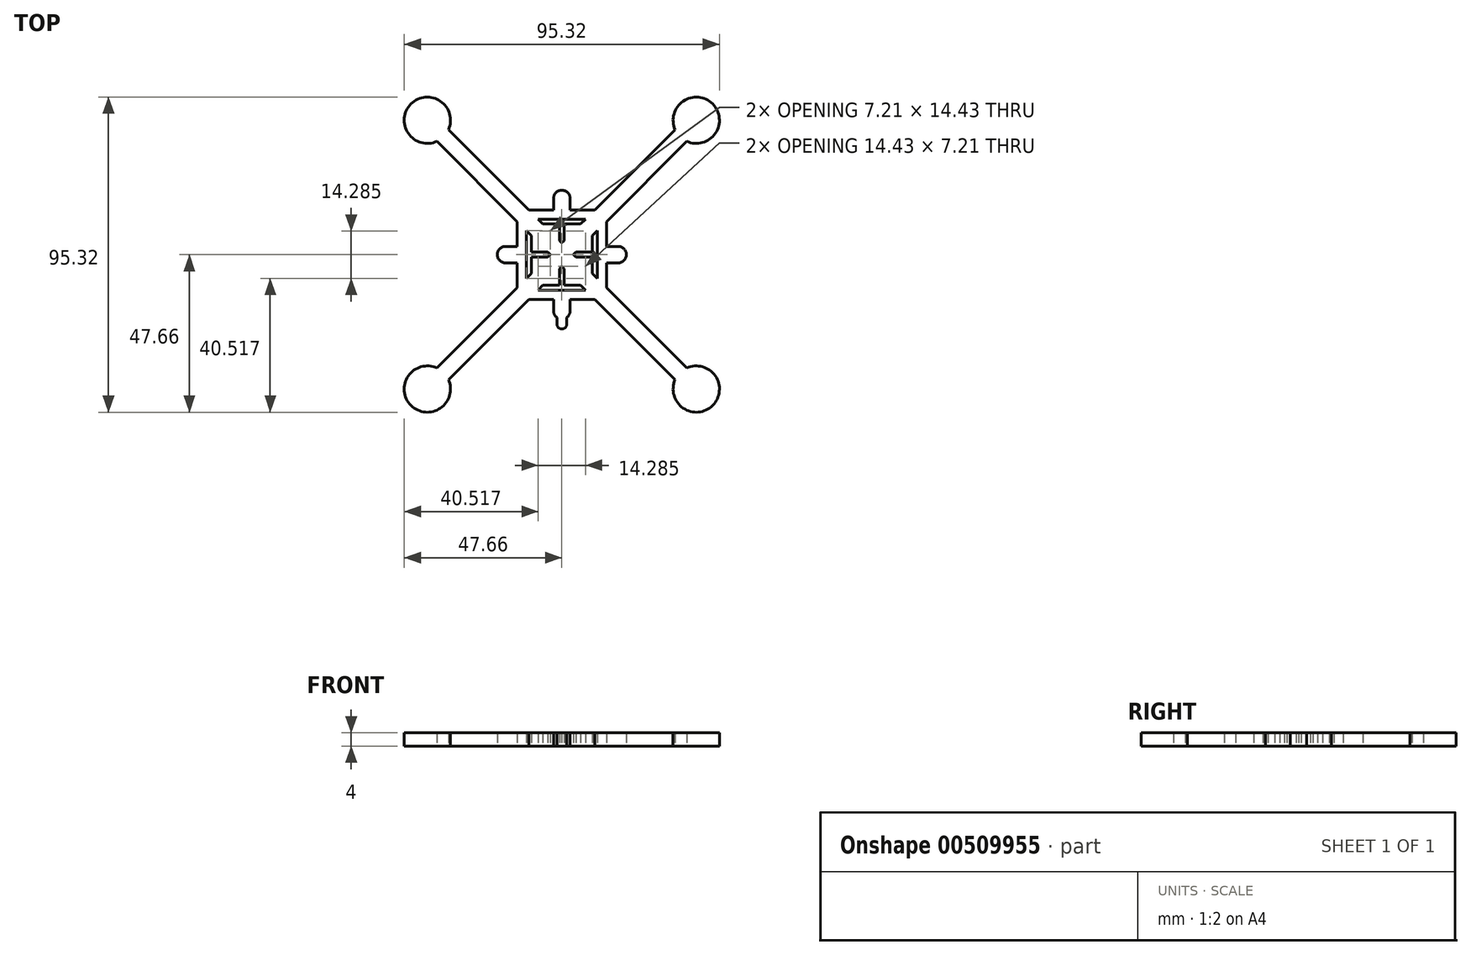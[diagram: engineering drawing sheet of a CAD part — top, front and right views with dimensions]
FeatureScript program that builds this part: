
annotation { "Feature Type Name" : "Feature", "Feature Type Description" : "" }
export const myFeature = defineFeature(function(context is Context, id is Id, definition is map)
    precondition{}
    {
        {
            var Q0;
            Q0=qCreatedBy(makeId("Top.planeOp"),FACE);
            var sketch = newSketch(context, id + "F0", { "sketchPlane" : qUnion([Q0])});
            skLineSegment(sketch, "E0", {"start": v(-40.66, 40.66) * mm, "end": v(40.66, -40.66) * mm});
            skLineSegment(sketch, "E1", {"start": v(40.66, 40.66) * mm, "end": v(-40.66, -40.66) * mm});
            skLineSegment(sketch, "E2.bottom", {"start": v(-13.5, 13.5) * mm, "end": v(13.5, 13.5) * mm});
            skLineSegment(sketch, "E2.top", {"start": v(-13.5, -13.5) * mm, "end": v(13.5, -13.5) * mm});
            skLineSegment(sketch, "E2.left", {"start": v(-13.5, 13.5) * mm, "end": v(-13.5, -13.5) * mm});
            skLineSegment(sketch, "E2.right", {"start": v(13.5, 13.5) * mm, "end": v(13.5, -13.5) * mm});
            skPoint(sketch, "E2.middle", {"position": v(0, 0) * mm});
            skCircle(sketch, "E3", {"center": v(-40.66, 40.66) * mm, "radius": 7 * mm});
            skCircle(sketch, "E4", {"center": v(-40.66, -40.66) * mm, "radius": 7 * mm});
            skCircle(sketch, "E5", {"center": v(40.66, -40.66) * mm, "radius": 7 * mm});
            skCircle(sketch, "E6", {"center": v(40.66, 40.66) * mm, "radius": 7 * mm});
            skPoint(sketch, "E7", {"position": v(-10, 10) * mm});
            skPoint(sketch, "E8", {"position": v(10, 10) * mm});
            skPoint(sketch, "E9", {"position": v(10, -10) * mm});
            skPoint(sketch, "E10", {"position": v(-10, -10) * mm});
            skCircle(sketch, "E11", {"center": v(0, 17) * mm, "radius": 1.5 * mm});
            skCircle(sketch, "E12", {"center": v(-17, 0) * mm, "radius": 1.5 * mm});
            skCircle(sketch, "E13", {"center": v(0, -17) * mm, "radius": 1.5 * mm});
            skCircle(sketch, "E14", {"center": v(0, -21) * mm, "radius": 1 * mm});
            skCircle(sketch, "E15", {"center": v(17, 0) * mm, "radius": 1.5 * mm});
            skCircle(sketch, "E16", {"center": v(0, 17) * mm, "radius": 2.5 * mm});
            skCircle(sketch, "E17", {"center": v(-17, 0) * mm, "radius": 2.5 * mm});
            skCircle(sketch, "E18", {"center": v(0, -17) * mm, "radius": 2.5 * mm});
            skCircle(sketch, "E19", {"center": v(17, 0) * mm, "radius": 2.5 * mm});
            skLineSegment(sketch, "E20", {"start": v(-2.5, 17) * mm, "end": v(-2.5, 13.5) * mm});
            skLineSegment(sketch, "E21", {"start": v(2.5, 17) * mm, "end": v(2.5, 13.5) * mm});
            skLineSegment(sketch, "E22", {"start": v(17, 2.5) * mm, "end": v(13.5, 2.5) * mm});
            skLineSegment(sketch, "E23", {"start": v(17, -2.5) * mm, "end": v(13.5, -2.5) * mm});
            skLineSegment(sketch, "E24", {"start": v(2.5, -17) * mm, "end": v(2.5, -13.5) * mm});
            skLineSegment(sketch, "E25", {"start": v(-2.5, -17) * mm, "end": v(-2.5, -13.5) * mm});
            skLineSegment(sketch, "E26", {"start": v(-17, -2.5) * mm, "end": v(-13.5, -2.5) * mm});
            skLineSegment(sketch, "E27", {"start": v(-17, 2.5) * mm, "end": v(-13.5, 2.5) * mm});
            skCircle(sketch, "E28", {"center": v(0, -21) * mm, "radius": 1.5 * mm});
            skLineSegment(sketch, "E29", {"start": v(-1.5, -21) * mm, "end": v(-1.5, -19) * mm});
            skLineSegment(sketch, "E30", {"start": v(1.5, -21) * mm, "end": v(1.5, -19) * mm});
            skLineSegment(sketch, "E31.0", {"start": v(38.9, 42.43) * mm, "end": v(-42.43, -38.9) * mm});
            skLineSegment(sketch, "E32.0", {"start": v(42.43, 38.9) * mm, "end": v(-38.9, -42.43) * mm});
            skLineSegment(sketch, "E33.0", {"start": v(-42.43, 38.9) * mm, "end": v(38.9, -42.43) * mm});
            skLineSegment(sketch, "E34.0", {"start": v(-38.9, 42.43) * mm, "end": v(42.43, -38.9) * mm});
            skLineSegment(sketch, "E35", {"start": v(-42.43, -38.9) * mm, "end": v(-40.66, -40.66) * mm});
            skLineSegment(sketch, "E36", {"start": v(-38.9, -42.43) * mm, "end": v(-40.66, -40.66) * mm});
            skLineSegment(sketch, "E37", {"start": v(38.9, 42.43) * mm, "end": v(40.66, 40.66) * mm});
            skLineSegment(sketch, "E38", {"start": v(40.66, 40.66) * mm, "end": v(42.43, 38.9) * mm});
            skLineSegment(sketch, "E39", {"start": v(42.43, -38.9) * mm, "end": v(40.66, -40.66) * mm});
            skLineSegment(sketch, "E40", {"start": v(40.66, -40.66) * mm, "end": v(38.9, -42.43) * mm});
            skLineSegment(sketch, "E41", {"start": v(-38.9, 42.43) * mm, "end": v(-40.66, 40.66) * mm});
            skLineSegment(sketch, "E42", {"start": v(-40.66, 40.66) * mm, "end": v(-42.43, 38.9) * mm});
            skPoint(sketch, "E43", {"position": v(-40.66, 45.16) * mm});
            skPoint(sketch, "E44.1.0", {"position": v(-45.16, 40.66) * mm});
            skPoint(sketch, "E44.2.0", {"position": v(-40.66, 36.16) * mm});
            skPoint(sketch, "E45.0.3.0", {"position": v(-36.16, 40.66) * mm});
            skPoint(sketch, "E46", {"position": v(40.66, 45.16) * mm});
            skPoint(sketch, "E47.1.0", {"position": v(36.16, 40.66) * mm});
            skPoint(sketch, "E47.2.0", {"position": v(40.66, 36.16) * mm});
            skLineSegment(sketch, "E47.anchor1", {"start": v(40.66, 40.66) * mm, "end": v(40.66, 45.16) * mm, "construction": true});
            skLineSegment(sketch, "E47.anchor2", {"start": v(40.66, 40.66) * mm, "end": v(45.16, 40.66) * mm, "construction": true});
            skPoint(sketch, "E48.0.3.0", {"position": v(45.16, 40.66) * mm});
            skPoint(sketch, "E49", {"position": v(40.66, -45.16) * mm});
            skPoint(sketch, "E50.1.0", {"position": v(36.16, -40.66) * mm});
            skPoint(sketch, "E50.2.0", {"position": v(40.66, -36.16) * mm});
            skPoint(sketch, "E50.3.0", {"position": v(45.16, -40.66) * mm});
            skLineSegment(sketch, "E50.anchor1", {"start": v(40.66, -40.66) * mm, "end": v(40.66, -45.16) * mm, "construction": true});
            skLineSegment(sketch, "E50.anchor2", {"start": v(40.66, -40.66) * mm, "end": v(45.16, -40.66) * mm, "construction": true});
            skPoint(sketch, "E51", {"position": v(-40.66, -45.16) * mm});
            skPoint(sketch, "E52.1.0", {"position": v(-45.16, -40.66) * mm});
            skPoint(sketch, "E52.2.0", {"position": v(-40.66, -36.16) * mm});
            skPoint(sketch, "E52.3.0", {"position": v(-36.16, -40.66) * mm});
            skLineSegment(sketch, "E52.anchor1", {"start": v(-40.66, -40.66) * mm, "end": v(-40.66, -45.16) * mm, "construction": true});
            skLineSegment(sketch, "E52.anchor2", {"start": v(-40.66, -40.66) * mm, "end": v(-36.16, -40.66) * mm, "construction": true});
            skLineSegment(sketch, "E53.bottom", {"start": v(10.75, -10.75) * mm, "end": v(-10.75, -10.75) * mm});
            skLineSegment(sketch, "E53.top", {"start": v(10.75, 10.75) * mm, "end": v(-10.75, 10.75) * mm});
            skLineSegment(sketch, "E53.left", {"start": v(10.75, -10.75) * mm, "end": v(10.75, 10.75) * mm});
            skLineSegment(sketch, "E53.right", {"start": v(-10.75, -10.75) * mm, "end": v(-10.75, 10.75) * mm});
            skLineSegment(sketch, "E54.bottom", {"start": v(-9.25, -9.25) * mm, "end": v(9.25, -9.25) * mm});
            skLineSegment(sketch, "E54.top", {"start": v(-9.25, 9.25) * mm, "end": v(9.25, 9.25) * mm});
            skLineSegment(sketch, "E54.left", {"start": v(-9.25, -9.25) * mm, "end": v(-9.25, 9.25) * mm});
            skLineSegment(sketch, "E54.right", {"start": v(9.25, -9.25) * mm, "end": v(9.25, 9.25) * mm});
            skLineSegment(sketch, "E55.bottom", {"start": v(-0.75, 9.25) * mm, "end": v(0.75, 9.25) * mm});
            skLineSegment(sketch, "E55.top", {"start": v(-0.75, -9.25) * mm, "end": v(0.75, -9.25) * mm});
            skLineSegment(sketch, "E55.left", {"start": v(-0.75, 9.25) * mm, "end": v(-0.75, -9.25) * mm});
            skLineSegment(sketch, "E55.right", {"start": v(0.75, 9.25) * mm, "end": v(0.75, -9.25) * mm});
            skLineSegment(sketch, "E56.bottom", {"start": v(-9.25, -0.75) * mm, "end": v(9.25, -0.75) * mm});
            skLineSegment(sketch, "E56.top", {"start": v(-9.25, 0.75) * mm, "end": v(9.25, 0.75) * mm});
            skLineSegment(sketch, "E56.left", {"start": v(-9.25, -0.75) * mm, "end": v(-9.25, 0.75) * mm});
            skLineSegment(sketch, "E56.right", {"start": v(9.25, -0.75) * mm, "end": v(9.25, 0.75) * mm});
            skPoint(sketch, "E56.cornerSnap0", {"position": v(-1.77, -0.75) * mm});
            skSolve(sketch);
        }
        {
            var Q0;
            {var subQ0=sQuery(id+"F0.wireOp",EDGE,"E39");Q0=makeQuery(id+"F0.imprint","IMPRINT",FACE,{"disambiguationData":[TD([[makeQuery(id+"F0.imprint","IMPRINT",EDGE,{"derivedFrom":subQ0}),1.0]])]});}
            var Q1;
            {var subQ3=sQuery(id+"F0.wireOp",EDGE,"E5");var subQ5=sQuery(id+"F0.wireOp",EDGE,"E33.0");var subQ7=makeQuery(id+"F0.imprint","INTERSECT",VERTEX,{"derivedFrom":[subQ3,subQ5]});Q1=makeQuery(id+"F0.imprint","IMPRINT",FACE,{"disambiguationData":[TD([[makeQuery(id+"F0.imprint","IMPRINT",EDGE,{"disambiguationData":[TD([[subQ7,1.0]])],"derivedFrom":subQ3}),-1.0]])]});}
            var Q2;
            {var subQ0=sQuery(id+"F0.wireOp",EDGE,"E56.bottom");var subQ1=sQuery(id+"F0.wireOp",EDGE,"E34.0");var subQ2=makeQuery(id+"F0.imprint","INTERSECT",VERTEX,{"derivedFrom":[subQ1,subQ0]});Q2=makeQuery(id+"F0.imprint","IMPRINT",FACE,{"disambiguationData":[TD([[makeQuery(id+"F0.imprint","IMPRINT",EDGE,{"disambiguationData":[TD([[subQ2,-1.0]])],"derivedFrom":subQ1}),1.0]])]});}
            var Q3;
            {var subQ3=sQuery(id+"F0.wireOp",EDGE,"E4");var subQ5=sQuery(id+"F0.wireOp",EDGE,"E32.0");var subQ6=makeQuery(id+"F0.imprint","INTERSECT",VERTEX,{"derivedFrom":[subQ3,subQ5]});Q3=makeQuery(id+"F0.imprint","IMPRINT",FACE,{"disambiguationData":[TD([[makeQuery(id+"F0.imprint","IMPRINT",EDGE,{"disambiguationData":[TD([[subQ6,-1.0]])],"derivedFrom":subQ3}),-1.0]])]});}
            var Q4;
            {var subQ0=sQuery(id+"F0.wireOp",EDGE,"E41");Q4=makeQuery(id+"F0.imprint","IMPRINT",FACE,{"disambiguationData":[TD([[makeQuery(id+"F0.imprint","IMPRINT",EDGE,{"derivedFrom":subQ0}),-1.0]])]});}
            var Q5;
            {var subQ3=sQuery(id+"F0.wireOp",EDGE,"E5");var subQ5=sQuery(id+"F0.wireOp",EDGE,"E34.0");var subQ7=makeQuery(id+"F0.imprint","INTERSECT",VERTEX,{"derivedFrom":[subQ3,subQ5]});Q5=makeQuery(id+"F0.imprint","IMPRINT",FACE,{"disambiguationData":[TD([[makeQuery(id+"F0.imprint","IMPRINT",EDGE,{"disambiguationData":[TD([[subQ7,-1.0]])],"derivedFrom":subQ3}),-1.0]])]});}
            var Q6;
            {var subQ3=sQuery(id+"F0.wireOp",EDGE,"E4");var subQ5=sQuery(id+"F0.wireOp",EDGE,"E31.0");var subQ7=makeQuery(id+"F0.imprint","INTERSECT",VERTEX,{"derivedFrom":[subQ3,subQ5]});Q6=makeQuery(id+"F0.imprint","IMPRINT",FACE,{"disambiguationData":[TD([[makeQuery(id+"F0.imprint","IMPRINT",EDGE,{"disambiguationData":[TD([[subQ7,1.0]])],"derivedFrom":subQ3}),-1.0]])]});}
            var Q7;
            {var subQ3=sQuery(id+"F0.wireOp",EDGE,"E31.0");var subQ5=sQuery(id+"F0.wireOp",EDGE,"E56.bottom");var subQ6=makeQuery(id+"F0.imprint","INTERSECT",VERTEX,{"derivedFrom":[subQ3,subQ5]});Q7=makeQuery(id+"F0.imprint","IMPRINT",FACE,{"disambiguationData":[TD([[makeQuery(id+"F0.imprint","IMPRINT",EDGE,{"disambiguationData":[TD([[subQ6,-1.0]])],"derivedFrom":subQ3}),1.0]])]});}
            var Q8;
            {var subQ1=sQuery(id+"F0.wireOp",EDGE,"E2.bottom");var subQ6=makeQuery(id+"F0.imprint","INTERSECT",VERTEX,{"derivedFrom":[subQ1,sQuery(id+"F0.wireOp",EDGE,"E20")]});Q8=makeQuery(id+"F0.imprint","IMPRINT",FACE,{"disambiguationData":[TD([[makeQuery(id+"F0.imprint","IMPRINT",EDGE,{"disambiguationData":[TD([[subQ6,1.0]])],"derivedFrom":subQ1}),-1.0]])]});}
            var Q9;
            {var subQ4=sQuery(id+"F0.wireOp",EDGE,"E35");Q9=makeQuery(id+"F0.imprint","IMPRINT",FACE,{"disambiguationData":[TD([[makeQuery(id+"F0.imprint","IMPRINT",EDGE,{"derivedFrom":subQ4}),-1.0]])]});}
            var Q10;
            {var subQ0=sQuery(id+"F0.wireOp",EDGE,"E56.right");Q10=makeQuery(id+"F0.imprint","IMPRINT",FACE,{"disambiguationData":[TD([[makeQuery(id+"F0.imprint","IMPRINT",EDGE,{"derivedFrom":subQ0}),-1.0]])]});}
            var Q11;
            {var subQ1=sQuery(id+"F0.wireOp",EDGE,"E2.right");var subQ8=makeQuery(id+"F0.imprint","INTERSECT",VERTEX,{"derivedFrom":[subQ1,sQuery(id+"F0.wireOp",EDGE,"E22")]});Q11=makeQuery(id+"F0.imprint","IMPRINT",FACE,{"disambiguationData":[TD([[makeQuery(id+"F0.imprint","IMPRINT",EDGE,{"disambiguationData":[TD([[subQ8,1.0]])],"derivedFrom":subQ1}),-1.0]])]});}
            var Q12;
            {var subQ0=sQuery(id+"F0.wireOp",EDGE,"E37");Q12=makeQuery(id+"F0.imprint","IMPRINT",FACE,{"disambiguationData":[TD([[makeQuery(id+"F0.imprint","IMPRINT",EDGE,{"derivedFrom":subQ0}),1.0]])]});}
            var Q13;
            {var subQ3=sQuery(id+"F0.wireOp",EDGE,"E6");var subQ5=sQuery(id+"F0.wireOp",EDGE,"E31.0");var subQ7=makeQuery(id+"F0.imprint","INTERSECT",VERTEX,{"derivedFrom":[subQ3,subQ5]});Q13=makeQuery(id+"F0.imprint","IMPRINT",FACE,{"disambiguationData":[TD([[makeQuery(id+"F0.imprint","IMPRINT",EDGE,{"disambiguationData":[TD([[subQ7,-1.0]])],"derivedFrom":subQ3}),-1.0]])]});}
            var Q14;
            {var subQ3=sQuery(id+"F0.wireOp",EDGE,"E3");var subQ5=sQuery(id+"F0.wireOp",EDGE,"E34.0");var subQ7=makeQuery(id+"F0.imprint","INTERSECT",VERTEX,{"derivedFrom":[subQ3,subQ5]});Q14=makeQuery(id+"F0.imprint","IMPRINT",FACE,{"disambiguationData":[TD([[makeQuery(id+"F0.imprint","IMPRINT",EDGE,{"disambiguationData":[TD([[subQ7,1.0]])],"derivedFrom":subQ3}),-1.0]])]});}
            var Q15;
            {var subQ3=sQuery(id+"F0.wireOp",EDGE,"E6");var subQ5=sQuery(id+"F0.wireOp",EDGE,"E32.0");var subQ7=makeQuery(id+"F0.imprint","INTERSECT",VERTEX,{"derivedFrom":[subQ3,subQ5]});Q15=makeQuery(id+"F0.imprint","IMPRINT",FACE,{"disambiguationData":[TD([[makeQuery(id+"F0.imprint","IMPRINT",EDGE,{"disambiguationData":[TD([[subQ7,1.0]])],"derivedFrom":subQ3}),-1.0]])]});}
            var Q16;
            {var subQ1=sQuery(id+"F0.wireOp",EDGE,"E0");var subQ7=sQuery(id+"F0.wireOp",EDGE,"E31.0");var subQ8=makeQuery(id+"F0.imprint","INTERSECT",VERTEX,{"derivedFrom":[subQ1,subQ7]});Q16=makeQuery(id+"F0.imprint","IMPRINT",FACE,{"disambiguationData":[TD([[makeQuery(id+"F0.imprint","IMPRINT",EDGE,{"disambiguationData":[TD([[subQ8,1.0]])],"derivedFrom":subQ7}),-1.0]])]});}
            var Q17;
            {var subQ1=sQuery(id+"F0.wireOp",EDGE,"E2.left");var subQ6=makeQuery(id+"F0.imprint","INTERSECT",VERTEX,{"derivedFrom":[subQ1,sQuery(id+"F0.wireOp",EDGE,"E27")]});Q17=makeQuery(id+"F0.imprint","IMPRINT",FACE,{"disambiguationData":[TD([[makeQuery(id+"F0.imprint","IMPRINT",EDGE,{"disambiguationData":[TD([[subQ6,1.0]])],"derivedFrom":subQ1}),1.0]])]});}
            var Q18;
            {var subQ3=sQuery(id+"F0.wireOp",EDGE,"E3");var subQ5=sQuery(id+"F0.wireOp",EDGE,"E33.0");var subQ7=makeQuery(id+"F0.imprint","INTERSECT",VERTEX,{"derivedFrom":[subQ3,subQ5]});Q18=makeQuery(id+"F0.imprint","IMPRINT",FACE,{"disambiguationData":[TD([[makeQuery(id+"F0.imprint","IMPRINT",EDGE,{"disambiguationData":[TD([[subQ7,-1.0]])],"derivedFrom":subQ3}),-1.0]])]});}
            var Q19;
            {var subQ1=sQuery(id+"F0.wireOp",EDGE,"E0");var subQ5=sQuery(id+"F0.wireOp",EDGE,"E32.0");var subQ6=makeQuery(id+"F0.imprint","INTERSECT",VERTEX,{"derivedFrom":[subQ1,subQ5]});Q19=makeQuery(id+"F0.imprint","IMPRINT",FACE,{"disambiguationData":[TD([[makeQuery(id+"F0.imprint","IMPRINT",EDGE,{"disambiguationData":[TD([[subQ6,1.0]])],"derivedFrom":subQ5}),1.0]])]});}
            var Q20;
            {var subQ1=sQuery(id+"F0.wireOp",EDGE,"E0");var subQ7=sQuery(id+"F0.wireOp",EDGE,"E32.0");var subQ8=makeQuery(id+"F0.imprint","INTERSECT",VERTEX,{"derivedFrom":[subQ1,subQ7]});Q20=makeQuery(id+"F0.imprint","IMPRINT",FACE,{"disambiguationData":[TD([[makeQuery(id+"F0.imprint","IMPRINT",EDGE,{"disambiguationData":[TD([[subQ8,-1.0]])],"derivedFrom":subQ7}),1.0]])]});}
            var Q21;
            {var subQ0=sQuery(id+"F0.wireOp",EDGE,"E55.right");var subQ1=sQuery(id+"F0.wireOp",EDGE,"E33.0");var subQ2=makeQuery(id+"F0.imprint","INTERSECT",VERTEX,{"derivedFrom":[subQ1,subQ0]});Q21=makeQuery(id+"F0.imprint","IMPRINT",FACE,{"disambiguationData":[TD([[makeQuery(id+"F0.imprint","IMPRINT",EDGE,{"disambiguationData":[TD([[subQ2,-1.0]])],"derivedFrom":subQ1}),-1.0]])]});}
            var Q22;
            {var subQ0=sQuery(id+"F0.wireOp",EDGE,"E55.left");var subQ1=sQuery(id+"F0.wireOp",EDGE,"E32.0");var subQ2=makeQuery(id+"F0.imprint","INTERSECT",VERTEX,{"derivedFrom":[subQ1,subQ0]});Q22=makeQuery(id+"F0.imprint","IMPRINT",FACE,{"disambiguationData":[TD([[makeQuery(id+"F0.imprint","IMPRINT",EDGE,{"disambiguationData":[TD([[subQ2,-1.0]])],"derivedFrom":subQ1}),1.0]])]});}
            var Q23;
            {var subQ3=sQuery(id+"F0.wireOp",EDGE,"E55.left");var subQ7=sQuery(id+"F0.wireOp",EDGE,"E32.0");var subQ9=makeQuery(id+"F0.imprint","INTERSECT",VERTEX,{"derivedFrom":[subQ7,subQ3]});Q23=makeQuery(id+"F0.imprint","IMPRINT",FACE,{"disambiguationData":[TD([[makeQuery(id+"F0.imprint","IMPRINT",EDGE,{"disambiguationData":[TD([[subQ9,-1.0]])],"derivedFrom":subQ7}),-1.0]])]});}
            var Q24;
            {var subQ5=sQuery(id+"F0.wireOp",EDGE,"E54.right");var subQ6=sQuery(id+"F0.wireOp",EDGE,"E32.0");var subQ7=makeQuery(id+"F0.imprint","INTERSECT",VERTEX,{"derivedFrom":[subQ6,subQ5]});Q24=makeQuery(id+"F0.imprint","IMPRINT",FACE,{"disambiguationData":[TD([[makeQuery(id+"F0.imprint","IMPRINT",EDGE,{"disambiguationData":[TD([[subQ7,-1.0]])],"derivedFrom":subQ6}),-1.0]])]});}
            var Q25;
            {var subQ0=sQuery(id+"F0.wireOp",EDGE,"E54.top");var subQ3=sQuery(id+"F0.wireOp",EDGE,"E31.0");var subQ4=makeQuery(id+"F0.imprint","INTERSECT",VERTEX,{"derivedFrom":[subQ3,subQ0]});Q25=makeQuery(id+"F0.imprint","IMPRINT",FACE,{"disambiguationData":[TD([[makeQuery(id+"F0.imprint","IMPRINT",EDGE,{"disambiguationData":[TD([[subQ4,-1.0]])],"derivedFrom":subQ3}),1.0]])]});}
            var Q26;
            {var subQ0=sQuery(id+"F0.wireOp",EDGE,"E54.top");var subQ1=sQuery(id+"F0.wireOp",EDGE,"E31.0");var subQ2=makeQuery(id+"F0.imprint","INTERSECT",VERTEX,{"derivedFrom":[subQ1,subQ0]});Q26=makeQuery(id+"F0.imprint","IMPRINT",FACE,{"disambiguationData":[TD([[makeQuery(id+"F0.imprint","IMPRINT",EDGE,{"disambiguationData":[TD([[subQ2,-1.0]])],"derivedFrom":subQ1}),-1.0]])]});}
            var Q27;
            Q27=makeQuery(id+"F0.imprint","IMPRINT",FACE,{"disambiguationData":[TD([[makeQuery(id+"F0.imprint","IMPRINT",EDGE,{"derivedFrom":sQuery(id+"F0.wireOp",EDGE,"E15")}),-1.0]])]});
            var Q28;
            {var subQ0=sQuery(id+"F0.wireOp",EDGE,"E56.right");Q28=makeQuery(id+"F0.imprint","IMPRINT",FACE,{"disambiguationData":[TD([[makeQuery(id+"F0.imprint","IMPRINT",EDGE,{"derivedFrom":subQ0}),1.0]])]});}
            var Q29;
            {var subQ0=sQuery(id+"F0.wireOp",EDGE,"E40");Q29=makeQuery(id+"F0.imprint","IMPRINT",FACE,{"disambiguationData":[TD([[makeQuery(id+"F0.imprint","IMPRINT",EDGE,{"derivedFrom":subQ0}),-1.0]])]});}
            var Q30;
            {var subQ3=sQuery(id+"F0.wireOp",EDGE,"E54.right");var subQ5=sQuery(id+"F0.wireOp",EDGE,"E34.0");var subQ6=makeQuery(id+"F0.imprint","INTERSECT",VERTEX,{"derivedFrom":[subQ5,subQ3]});Q30=makeQuery(id+"F0.imprint","IMPRINT",FACE,{"disambiguationData":[TD([[makeQuery(id+"F0.imprint","IMPRINT",EDGE,{"disambiguationData":[TD([[subQ6,-1.0]])],"derivedFrom":subQ5}),-1.0]])]});}
            var Q31;
            {var subQ0=sQuery(id+"F0.wireOp",EDGE,"E36");Q31=makeQuery(id+"F0.imprint","IMPRINT",FACE,{"disambiguationData":[TD([[makeQuery(id+"F0.imprint","IMPRINT",EDGE,{"derivedFrom":subQ0}),-1.0]])]});}
            var Q32;
            {var subQ0=sQuery(id+"F0.wireOp",EDGE,"E35");Q32=makeQuery(id+"F0.imprint","IMPRINT",FACE,{"disambiguationData":[TD([[makeQuery(id+"F0.imprint","IMPRINT",EDGE,{"derivedFrom":subQ0}),1.0]])]});}
            var Q33;
            {var subQ0=sQuery(id+"F0.wireOp",EDGE,"E24");Q33=makeQuery(id+"F0.imprint","IMPRINT",FACE,{"disambiguationData":[TD([[makeQuery(id+"F0.imprint","IMPRINT",EDGE,{"derivedFrom":subQ0}),1.0]])]});}
            var Q34;
            {var subQ0=sQuery(id+"F0.wireOp",EDGE,"E55.top");Q34=makeQuery(id+"F0.imprint","IMPRINT",FACE,{"disambiguationData":[TD([[makeQuery(id+"F0.imprint","IMPRINT",EDGE,{"derivedFrom":subQ0}),-1.0]])]});}
            var Q35;
            Q35=makeQuery(id+"F0.imprint","IMPRINT",FACE,{"disambiguationData":[TD([[makeQuery(id+"F0.imprint","IMPRINT",EDGE,{"derivedFrom":sQuery(id+"F0.wireOp",EDGE,"E11")}),-1.0]])]});
            var Q36;
            {var subQ0=sQuery(id+"F0.wireOp",EDGE,"E56.left");Q36=makeQuery(id+"F0.imprint","IMPRINT",FACE,{"disambiguationData":[TD([[makeQuery(id+"F0.imprint","IMPRINT",EDGE,{"derivedFrom":subQ0}),-1.0]])]});}
            var Q37;
            {var subQ0=sQuery(id+"F0.wireOp",EDGE,"E55.right");var subQ1=sQuery(id+"F0.wireOp",EDGE,"E31.0");var subQ2=makeQuery(id+"F0.imprint","INTERSECT",VERTEX,{"derivedFrom":[subQ1,subQ0]});Q37=makeQuery(id+"F0.imprint","IMPRINT",FACE,{"disambiguationData":[TD([[makeQuery(id+"F0.imprint","IMPRINT",EDGE,{"disambiguationData":[TD([[subQ2,-1.0]])],"derivedFrom":subQ1}),1.0]])]});}
            var Q38;
            {var subQ0=sQuery(id+"F0.wireOp",EDGE,"E54.top");var subQ1=sQuery(id+"F0.wireOp",EDGE,"E34.0");var subQ2=makeQuery(id+"F0.imprint","INTERSECT",VERTEX,{"derivedFrom":[subQ1,subQ0]});Q38=makeQuery(id+"F0.imprint","IMPRINT",FACE,{"disambiguationData":[TD([[makeQuery(id+"F0.imprint","IMPRINT",EDGE,{"disambiguationData":[TD([[subQ2,-1.0]])],"derivedFrom":subQ1}),1.0]])]});}
            var Q39;
            {var subQ0=sQuery(id+"F0.wireOp",EDGE,"E39");Q39=makeQuery(id+"F0.imprint","IMPRINT",FACE,{"disambiguationData":[TD([[makeQuery(id+"F0.imprint","IMPRINT",EDGE,{"derivedFrom":subQ0}),-1.0]])]});}
            var Q40;
            {var subQ0=sQuery(id+"F0.wireOp",EDGE,"E37");Q40=makeQuery(id+"F0.imprint","IMPRINT",FACE,{"disambiguationData":[TD([[makeQuery(id+"F0.imprint","IMPRINT",EDGE,{"derivedFrom":subQ0}),-1.0]])]});}
            var Q41;
            {var subQ0=sQuery(id+"F0.wireOp",EDGE,"E2.bottom");var subQ5=sQuery(id+"F0.wireOp",EDGE,"E34.0");var subQ6=makeQuery(id+"F0.imprint","INTERSECT",VERTEX,{"derivedFrom":[subQ0,subQ5]});Q41=makeQuery(id+"F0.imprint","IMPRINT",FACE,{"disambiguationData":[TD([[makeQuery(id+"F0.imprint","IMPRINT",EDGE,{"disambiguationData":[TD([[subQ6,-1.0]])],"derivedFrom":subQ5}),-1.0]])]});}
            var Q42;
            {var subQ0=sQuery(id+"F0.wireOp",EDGE,"E26");Q42=makeQuery(id+"F0.imprint","IMPRINT",FACE,{"disambiguationData":[TD([[makeQuery(id+"F0.imprint","IMPRINT",EDGE,{"derivedFrom":subQ0}),1.0]])]});}
            var Q43;
            {var subQ0=sQuery(id+"F0.wireOp",EDGE,"E20");Q43=makeQuery(id+"F0.imprint","IMPRINT",FACE,{"disambiguationData":[TD([[makeQuery(id+"F0.imprint","IMPRINT",EDGE,{"derivedFrom":subQ0}),1.0]])]});}
            var Q44;
            {var subQ0=sQuery(id+"F0.wireOp",EDGE,"E53.left");var subQ5=sQuery(id+"F0.wireOp",EDGE,"E32.0");var subQ6=makeQuery(id+"F0.imprint","INTERSECT",VERTEX,{"derivedFrom":[subQ5,subQ0]});Q44=makeQuery(id+"F0.imprint","IMPRINT",FACE,{"disambiguationData":[TD([[makeQuery(id+"F0.imprint","IMPRINT",EDGE,{"disambiguationData":[TD([[subQ6,-1.0]])],"derivedFrom":subQ5}),-1.0]])]});}
            var Q45;
            {var subQ0=sQuery(id+"F0.wireOp",EDGE,"E2.right");var subQ5=sQuery(id+"F0.wireOp",EDGE,"E32.0");var subQ6=makeQuery(id+"F0.imprint","INTERSECT",VERTEX,{"derivedFrom":[subQ0,subQ5]});Q45=makeQuery(id+"F0.imprint","IMPRINT",FACE,{"disambiguationData":[TD([[makeQuery(id+"F0.imprint","IMPRINT",EDGE,{"disambiguationData":[TD([[subQ6,-1.0]])],"derivedFrom":subQ5}),-1.0]])]});}
            var Q46;
            {var subQ0=sQuery(id+"F0.wireOp",EDGE,"E2.bottom");var subQ5=sQuery(id+"F0.wireOp",EDGE,"E31.0");var subQ6=makeQuery(id+"F0.imprint","INTERSECT",VERTEX,{"derivedFrom":[subQ0,subQ5]});Q46=makeQuery(id+"F0.imprint","IMPRINT",FACE,{"disambiguationData":[TD([[makeQuery(id+"F0.imprint","IMPRINT",EDGE,{"disambiguationData":[TD([[subQ6,-1.0]])],"derivedFrom":subQ5}),1.0]])]});}
            var Q47;
            {var subQ0=sQuery(id+"F0.wireOp",EDGE,"E38");Q47=makeQuery(id+"F0.imprint","IMPRINT",FACE,{"disambiguationData":[TD([[makeQuery(id+"F0.imprint","IMPRINT",EDGE,{"derivedFrom":subQ0}),-1.0]])]});}
            var Q48;
            {var subQ0=sQuery(id+"F0.wireOp",EDGE,"E2.left");var subQ5=sQuery(id+"F0.wireOp",EDGE,"E33.0");var subQ7=makeQuery(id+"F0.imprint","INTERSECT",VERTEX,{"derivedFrom":[subQ0,subQ5]});Q48=makeQuery(id+"F0.imprint","IMPRINT",FACE,{"disambiguationData":[TD([[makeQuery(id+"F0.imprint","IMPRINT",EDGE,{"disambiguationData":[TD([[subQ7,-1.0]])],"derivedFrom":subQ5}),1.0]])]});}
            var Q49;
            {var subQ3=sQuery(id+"F0.wireOp",EDGE,"E54.bottom");var subQ5=sQuery(id+"F0.wireOp",EDGE,"E33.0");var subQ6=makeQuery(id+"F0.imprint","INTERSECT",VERTEX,{"derivedFrom":[subQ5,subQ3]});Q49=makeQuery(id+"F0.imprint","IMPRINT",FACE,{"disambiguationData":[TD([[makeQuery(id+"F0.imprint","IMPRINT",EDGE,{"disambiguationData":[TD([[subQ6,-1.0]])],"derivedFrom":subQ5}),1.0]])]});}
            var Q50;
            {var subQ1=sQuery(id+"F0.wireOp",EDGE,"E2.top");var subQ9=makeQuery(id+"F0.imprint","INTERSECT",VERTEX,{"derivedFrom":[subQ1,sQuery(id+"F0.wireOp",EDGE,"E25")]});Q50=makeQuery(id+"F0.imprint","IMPRINT",FACE,{"disambiguationData":[TD([[makeQuery(id+"F0.imprint","IMPRINT",EDGE,{"disambiguationData":[TD([[subQ9,1.0]])],"derivedFrom":subQ1}),1.0]])]});}
            var Q51;
            {var subQ0=sQuery(id+"F0.wireOp",EDGE,"E42");Q51=makeQuery(id+"F0.imprint","IMPRINT",FACE,{"disambiguationData":[TD([[makeQuery(id+"F0.imprint","IMPRINT",EDGE,{"derivedFrom":subQ0}),1.0]])]});}
            var Q52;
            {var subQ0=sQuery(id+"F0.wireOp",EDGE,"E41");Q52=makeQuery(id+"F0.imprint","IMPRINT",FACE,{"disambiguationData":[TD([[makeQuery(id+"F0.imprint","IMPRINT",EDGE,{"derivedFrom":subQ0}),1.0]])]});}
            var Q53;
            {var subQ1=sQuery(id+"F0.wireOp",EDGE,"E55.top");Q53=makeQuery(id+"F0.imprint","IMPRINT",FACE,{"disambiguationData":[TD([[makeQuery(id+"F0.imprint","IMPRINT",EDGE,{"derivedFrom":subQ1}),1.0]])]});}
            var Q54;
            {var subQ0=sQuery(id+"F0.wireOp",EDGE,"E33.0");var subQ1=sQuery(id+"F0.wireOp",EDGE,"E32.0");var subQ2=makeQuery(id+"F0.imprint","INTERSECT",VERTEX,{"derivedFrom":[subQ1,subQ0]});Q54=makeQuery(id+"F0.imprint","IMPRINT",FACE,{"disambiguationData":[TD([[makeQuery(id+"F0.imprint","IMPRINT",EDGE,{"disambiguationData":[TD([[subQ2,-1.0]])],"derivedFrom":subQ1}),-1.0]])]});}
            var Q55;
            {var subQ1=sQuery(id+"F0.wireOp",EDGE,"E55.bottom");Q55=makeQuery(id+"F0.imprint","IMPRINT",FACE,{"disambiguationData":[TD([[makeQuery(id+"F0.imprint","IMPRINT",EDGE,{"derivedFrom":subQ1}),-1.0]])]});}
            var Q56;
            {var subQ0=sQuery(id+"F0.wireOp",EDGE,"E53.right");var subQ5=sQuery(id+"F0.wireOp",EDGE,"E33.0");var subQ6=makeQuery(id+"F0.imprint","INTERSECT",VERTEX,{"derivedFrom":[subQ5,subQ0]});Q56=makeQuery(id+"F0.imprint","IMPRINT",FACE,{"disambiguationData":[TD([[makeQuery(id+"F0.imprint","IMPRINT",EDGE,{"disambiguationData":[TD([[subQ6,-1.0]])],"derivedFrom":subQ5}),1.0]])]});}
            var Q57;
            {var subQ0=sQuery(id+"F0.wireOp",EDGE,"E54.left");var subQ1=sQuery(id+"F0.wireOp",EDGE,"E33.0");var subQ2=makeQuery(id+"F0.imprint","INTERSECT",VERTEX,{"derivedFrom":[subQ1,subQ0]});Q57=makeQuery(id+"F0.imprint","IMPRINT",FACE,{"disambiguationData":[TD([[makeQuery(id+"F0.imprint","IMPRINT",EDGE,{"disambiguationData":[TD([[subQ2,-1.0]])],"derivedFrom":subQ1}),-1.0]])]});}
            var Q58;
            {var subQ0=sQuery(id+"F0.wireOp",EDGE,"E56.bottom");var subQ1=sQuery(id+"F0.wireOp",EDGE,"E31.0");var subQ2=makeQuery(id+"F0.imprint","INTERSECT",VERTEX,{"derivedFrom":[subQ1,subQ0]});Q58=makeQuery(id+"F0.imprint","IMPRINT",FACE,{"disambiguationData":[TD([[makeQuery(id+"F0.imprint","IMPRINT",EDGE,{"disambiguationData":[TD([[subQ2,-1.0]])],"derivedFrom":subQ1}),-1.0]])]});}
            var Q59;
            {var subQ5=sQuery(id+"F0.wireOp",EDGE,"E0");var subQ7=sQuery(id+"F0.wireOp",EDGE,"E31.0");var subQ8=makeQuery(id+"F0.imprint","INTERSECT",VERTEX,{"derivedFrom":[subQ5,subQ7]});Q59=makeQuery(id+"F0.imprint","IMPRINT",FACE,{"disambiguationData":[TD([[makeQuery(id+"F0.imprint","IMPRINT",EDGE,{"disambiguationData":[TD([[subQ8,-1.0]])],"derivedFrom":subQ7}),-1.0]])]});}
            var Q60;
            {var subQ3=sQuery(id+"F0.wireOp",EDGE,"E54.left");var subQ5=sQuery(id+"F0.wireOp",EDGE,"E31.0");var subQ6=makeQuery(id+"F0.imprint","INTERSECT",VERTEX,{"derivedFrom":[subQ5,subQ3]});Q60=makeQuery(id+"F0.imprint","IMPRINT",FACE,{"disambiguationData":[TD([[makeQuery(id+"F0.imprint","IMPRINT",EDGE,{"disambiguationData":[TD([[subQ6,-1.0]])],"derivedFrom":subQ5}),1.0]])]});}
            var Q61;
            {var subQ0=sQuery(id+"F0.wireOp",EDGE,"E56.left");Q61=makeQuery(id+"F0.imprint","IMPRINT",FACE,{"disambiguationData":[TD([[makeQuery(id+"F0.imprint","IMPRINT",EDGE,{"derivedFrom":subQ0}),1.0]])]});}
            var Q62;
            {var subQ0=sQuery(id+"F0.wireOp",EDGE,"E53.top");var subQ5=sQuery(id+"F0.wireOp",EDGE,"E31.0");var subQ6=makeQuery(id+"F0.imprint","INTERSECT",VERTEX,{"derivedFrom":[subQ5,subQ0]});Q62=makeQuery(id+"F0.imprint","IMPRINT",FACE,{"disambiguationData":[TD([[makeQuery(id+"F0.imprint","IMPRINT",EDGE,{"disambiguationData":[TD([[subQ6,-1.0]])],"derivedFrom":subQ5}),1.0]])]});}
            var Q63;
            {var subQ0=sQuery(id+"F0.wireOp",EDGE,"E55.bottom");Q63=makeQuery(id+"F0.imprint","IMPRINT",FACE,{"disambiguationData":[TD([[makeQuery(id+"F0.imprint","IMPRINT",EDGE,{"derivedFrom":subQ0}),1.0]])]});}
            var Q64;
            {var subQ0=sQuery(id+"F0.wireOp",EDGE,"E54.right");var subQ1=sQuery(id+"F0.wireOp",EDGE,"E32.0");var subQ2=makeQuery(id+"F0.imprint","INTERSECT",VERTEX,{"derivedFrom":[subQ1,subQ0]});Q64=makeQuery(id+"F0.imprint","IMPRINT",FACE,{"disambiguationData":[TD([[makeQuery(id+"F0.imprint","IMPRINT",EDGE,{"disambiguationData":[TD([[subQ2,-1.0]])],"derivedFrom":subQ1}),1.0]])]});}
            var Q65;
            Q65=makeQuery(id+"F0.imprint","IMPRINT",FACE,{"disambiguationData":[TD([[makeQuery(id+"F0.imprint","IMPRINT",EDGE,{"derivedFrom":sQuery(id+"F0.wireOp",EDGE,"E12")}),-1.0]])]});
            var Q66;
            Q66=makeQuery(id+"F0.imprint","IMPRINT",FACE,{"disambiguationData":[TD([[makeQuery(id+"F0.imprint","IMPRINT",EDGE,{"derivedFrom":sQuery(id+"F0.wireOp",EDGE,"E15")}),1.0]])]});
            var Q67;
            Q67=makeQuery(id+"F0.imprint","IMPRINT",FACE,{"disambiguationData":[TD([[makeQuery(id+"F0.imprint","IMPRINT",EDGE,{"derivedFrom":sQuery(id+"F0.wireOp",EDGE,"E11")}),1.0]])]});
            var Q68;
            {var subQ0=sQuery(id+"F0.wireOp",EDGE,"E2.right");var subQ5=sQuery(id+"F0.wireOp",EDGE,"E34.0");var subQ6=makeQuery(id+"F0.imprint","INTERSECT",VERTEX,{"derivedFrom":[subQ0,subQ5]});Q68=makeQuery(id+"F0.imprint","IMPRINT",FACE,{"disambiguationData":[TD([[makeQuery(id+"F0.imprint","IMPRINT",EDGE,{"disambiguationData":[TD([[subQ6,1.0]])],"derivedFrom":subQ5}),-1.0]])]});}
            var Q69;
            {var subQ0=sQuery(id+"F0.wireOp",EDGE,"E22");Q69=makeQuery(id+"F0.imprint","IMPRINT",FACE,{"disambiguationData":[TD([[makeQuery(id+"F0.imprint","IMPRINT",EDGE,{"derivedFrom":subQ0}),1.0]])]});}
            var Q70;
            {var subQ3=sQuery(id+"F0.wireOp",EDGE,"E54.bottom");var subQ5=sQuery(id+"F0.wireOp",EDGE,"E32.0");var subQ6=makeQuery(id+"F0.imprint","INTERSECT",VERTEX,{"derivedFrom":[subQ5,subQ3]});Q70=makeQuery(id+"F0.imprint","IMPRINT",FACE,{"disambiguationData":[TD([[makeQuery(id+"F0.imprint","IMPRINT",EDGE,{"disambiguationData":[TD([[subQ6,-1.0]])],"derivedFrom":subQ5}),-1.0]])]});}
            var Q71;
            Q71=makeQuery(id+"F0.imprint","IMPRINT",FACE,{"disambiguationData":[TD([[makeQuery(id+"F0.imprint","IMPRINT",EDGE,{"derivedFrom":sQuery(id+"F0.wireOp",EDGE,"E13")}),-1.0]])]});
            var Q72;
            {var subQ0=sQuery(id+"F0.wireOp",EDGE,"E2.top");var subQ5=sQuery(id+"F0.wireOp",EDGE,"E32.0");var subQ6=makeQuery(id+"F0.imprint","INTERSECT",VERTEX,{"derivedFrom":[subQ0,subQ5]});Q72=makeQuery(id+"F0.imprint","IMPRINT",FACE,{"disambiguationData":[TD([[makeQuery(id+"F0.imprint","IMPRINT",EDGE,{"disambiguationData":[TD([[subQ6,1.0]])],"derivedFrom":subQ5}),-1.0]])]});}
            var Q73;
            {var subQ0=sQuery(id+"F0.wireOp",EDGE,"E55.right");var subQ1=sQuery(id+"F0.wireOp",EDGE,"E32.0");var subQ2=makeQuery(id+"F0.imprint","INTERSECT",VERTEX,{"derivedFrom":[subQ1,subQ0]});Q73=makeQuery(id+"F0.imprint","IMPRINT",FACE,{"disambiguationData":[TD([[makeQuery(id+"F0.imprint","IMPRINT",EDGE,{"disambiguationData":[TD([[subQ2,-1.0]])],"derivedFrom":subQ1}),1.0]])]});}
            var Q74;
            {var subQ0=sQuery(id+"F0.wireOp",EDGE,"E34.0");var subQ1=sQuery(id+"F0.wireOp",EDGE,"E31.0");var subQ2=makeQuery(id+"F0.imprint","INTERSECT",VERTEX,{"derivedFrom":[subQ1,subQ0]});Q74=makeQuery(id+"F0.imprint","IMPRINT",FACE,{"disambiguationData":[TD([[makeQuery(id+"F0.imprint","IMPRINT",EDGE,{"disambiguationData":[TD([[subQ2,-1.0]])],"derivedFrom":subQ1}),-1.0]])]});}
            var Q75;
            {var subQ0=sQuery(id+"F0.wireOp",EDGE,"E53.top");var subQ5=sQuery(id+"F0.wireOp",EDGE,"E34.0");var subQ6=makeQuery(id+"F0.imprint","INTERSECT",VERTEX,{"derivedFrom":[subQ5,subQ0]});Q75=makeQuery(id+"F0.imprint","IMPRINT",FACE,{"disambiguationData":[TD([[makeQuery(id+"F0.imprint","IMPRINT",EDGE,{"disambiguationData":[TD([[subQ6,-1.0]])],"derivedFrom":subQ5}),-1.0]])]});}
            var Q76;
            {var subQ0=sQuery(id+"F0.wireOp",EDGE,"E34.0");var subQ1=sQuery(id+"F0.wireOp",EDGE,"E32.0");var subQ2=makeQuery(id+"F0.imprint","INTERSECT",VERTEX,{"derivedFrom":[subQ1,subQ0]});Q76=makeQuery(id+"F0.imprint","IMPRINT",FACE,{"disambiguationData":[TD([[makeQuery(id+"F0.imprint","IMPRINT",EDGE,{"disambiguationData":[TD([[subQ2,-1.0]])],"derivedFrom":subQ1}),1.0]])]});}
            var Q77;
            {var subQ0=sQuery(id+"F0.wireOp",EDGE,"E56.top");var subQ1=sQuery(id+"F0.wireOp",EDGE,"E32.0");var subQ2=makeQuery(id+"F0.imprint","INTERSECT",VERTEX,{"derivedFrom":[subQ1,subQ0]});Q77=makeQuery(id+"F0.imprint","IMPRINT",FACE,{"disambiguationData":[TD([[makeQuery(id+"F0.imprint","IMPRINT",EDGE,{"disambiguationData":[TD([[subQ2,-1.0]])],"derivedFrom":subQ1}),-1.0]])]});}
            var Q78;
            Q78=makeQuery(id+"F0.imprint","IMPRINT",FACE,{"disambiguationData":[TD([[makeQuery(id+"F0.imprint","IMPRINT",EDGE,{"derivedFrom":sQuery(id+"F0.wireOp",EDGE,"E14")}),1.0]])]});
            var Q79;
            Q79=makeQuery(id+"F0.imprint","IMPRINT",FACE,{"disambiguationData":[TD([[makeQuery(id+"F0.imprint","IMPRINT",EDGE,{"derivedFrom":sQuery(id+"F0.wireOp",EDGE,"E12")}),1.0]])]});
            var Q80;
            Q80=makeQuery(id+"F0.imprint","IMPRINT",FACE,{"disambiguationData":[TD([[makeQuery(id+"F0.imprint","IMPRINT",EDGE,{"derivedFrom":sQuery(id+"F0.wireOp",EDGE,"E14")}),-1.0]])]});
            var Q81;
            {var subQ0=sQuery(id+"F0.wireOp",EDGE,"E29");Q81=makeQuery(id+"F0.imprint","IMPRINT",FACE,{"disambiguationData":[TD([[makeQuery(id+"F0.imprint","IMPRINT",EDGE,{"derivedFrom":subQ0}),-1.0]])]});}
            var Q82;
            {var subQ0=sQuery(id+"F0.wireOp",EDGE,"E2.top");var subQ5=sQuery(id+"F0.wireOp",EDGE,"E33.0");var subQ7=makeQuery(id+"F0.imprint","INTERSECT",VERTEX,{"derivedFrom":[subQ0,subQ5]});Q82=makeQuery(id+"F0.imprint","IMPRINT",FACE,{"disambiguationData":[TD([[makeQuery(id+"F0.imprint","IMPRINT",EDGE,{"disambiguationData":[TD([[subQ7,1.0]])],"derivedFrom":subQ5}),1.0]])]});}
            var Q83;
            {var subQ0=sQuery(id+"F0.wireOp",EDGE,"E30");Q83=makeQuery(id+"F0.imprint","IMPRINT",FACE,{"disambiguationData":[TD([[makeQuery(id+"F0.imprint","IMPRINT",EDGE,{"derivedFrom":subQ0}),1.0]])]});}
            var Q84;
            {var subQ0=sQuery(id+"F0.wireOp",EDGE,"E2.left");var subQ5=sQuery(id+"F0.wireOp",EDGE,"E31.0");var subQ7=makeQuery(id+"F0.imprint","INTERSECT",VERTEX,{"derivedFrom":[subQ0,subQ5]});Q84=makeQuery(id+"F0.imprint","IMPRINT",FACE,{"disambiguationData":[TD([[makeQuery(id+"F0.imprint","IMPRINT",EDGE,{"disambiguationData":[TD([[subQ7,1.0]])],"derivedFrom":subQ5}),1.0]])]});}
            var Q85;
            Q85=makeQuery(id+"F0.imprint","IMPRINT",FACE,{"disambiguationData":[TD([[makeQuery(id+"F0.imprint","IMPRINT",EDGE,{"derivedFrom":sQuery(id+"F0.wireOp",EDGE,"E13")}),1.0]])]});
            var Q86;
            {var subQ0=sQuery(id+"F0.wireOp",EDGE,"E32.0");var subQ1=sQuery(id+"F0.wireOp",EDGE,"E0");var subQ2=makeQuery(id+"F0.imprint","INTERSECT",VERTEX,{"derivedFrom":[subQ1,subQ0]});Q86=makeQuery(id+"F0.imprint","IMPRINT",FACE,{"disambiguationData":[TD([[makeQuery(id+"F0.imprint","IMPRINT",EDGE,{"disambiguationData":[TD([[subQ2,1.0]])],"derivedFrom":subQ0}),-1.0]])]});}
            var Q87;
            {var subQ0=sQuery(id+"F0.wireOp",EDGE,"E31.0");var subQ1=sQuery(id+"F0.wireOp",EDGE,"E0");var subQ2=makeQuery(id+"F0.imprint","INTERSECT",VERTEX,{"derivedFrom":[subQ1,subQ0]});Q87=makeQuery(id+"F0.imprint","IMPRINT",FACE,{"disambiguationData":[TD([[makeQuery(id+"F0.imprint","IMPRINT",EDGE,{"disambiguationData":[TD([[subQ2,1.0]])],"derivedFrom":subQ0}),1.0]])]});}
            var Q88;
            {var subQ0=sQuery(id+"F0.wireOp",EDGE,"E33.0");var subQ1=sQuery(id+"F0.wireOp",EDGE,"E1");var subQ2=makeQuery(id+"F0.imprint","INTERSECT",VERTEX,{"derivedFrom":[subQ1,subQ0]});Q88=makeQuery(id+"F0.imprint","IMPRINT",FACE,{"disambiguationData":[TD([[makeQuery(id+"F0.imprint","IMPRINT",EDGE,{"disambiguationData":[TD([[subQ2,-1.0]])],"derivedFrom":subQ0}),1.0]])]});}
            var Q89;
            {var subQ0=sQuery(id+"F0.wireOp",EDGE,"E33.0");var subQ1=sQuery(id+"F0.wireOp",EDGE,"E1");var subQ2=makeQuery(id+"F0.imprint","INTERSECT",VERTEX,{"derivedFrom":[subQ1,subQ0]});Q89=makeQuery(id+"F0.imprint","IMPRINT",FACE,{"disambiguationData":[TD([[makeQuery(id+"F0.imprint","IMPRINT",EDGE,{"disambiguationData":[TD([[subQ2,1.0]])],"derivedFrom":subQ0}),1.0]])]});}
            var Q90;
            {var subQ0=sQuery(id+"F0.wireOp",EDGE,"E56.top");var subQ1=sQuery(id+"F0.wireOp",EDGE,"E31.0");var subQ2=makeQuery(id+"F0.imprint","INTERSECT",VERTEX,{"derivedFrom":[subQ1,subQ0]});Q90=makeQuery(id+"F0.imprint","IMPRINT",FACE,{"disambiguationData":[TD([[makeQuery(id+"F0.imprint","IMPRINT",EDGE,{"disambiguationData":[TD([[subQ2,-1.0]])],"derivedFrom":subQ1}),-1.0]])]});}
            var Q91;
            {var subQ0=sQuery(id+"F0.wireOp",EDGE,"E55.right");var subQ1=sQuery(id+"F0.wireOp",EDGE,"E32.0");var subQ2=makeQuery(id+"F0.imprint","INTERSECT",VERTEX,{"derivedFrom":[subQ1,subQ0]});Q91=makeQuery(id+"F0.imprint","IMPRINT",FACE,{"disambiguationData":[TD([[makeQuery(id+"F0.imprint","IMPRINT",EDGE,{"disambiguationData":[TD([[subQ2,-1.0]])],"derivedFrom":subQ1}),-1.0]])]});}
            var Q92;
            {var subQ0=sQuery(id+"F0.wireOp",EDGE,"E1");var subQ1=sQuery(id+"F0.wireOp",EDGE,"E0");var subQ2=makeQuery(id+"F0.imprint","INTERSECT",VERTEX,{"derivedFrom":[subQ1,subQ0]});Q92=makeQuery(id+"F0.imprint","IMPRINT",FACE,{"disambiguationData":[TD([[makeQuery(id+"F0.imprint","IMPRINT",EDGE,{"disambiguationData":[TD([[subQ2,1.0]])],"derivedFrom":subQ1}),1.0]])]});}
            var Q93;
            {var subQ0=sQuery(id+"F0.wireOp",EDGE,"E1");var subQ1=sQuery(id+"F0.wireOp",EDGE,"E0");var subQ2=makeQuery(id+"F0.imprint","INTERSECT",VERTEX,{"derivedFrom":[subQ1,subQ0]});Q93=makeQuery(id+"F0.imprint","IMPRINT",FACE,{"disambiguationData":[TD([[makeQuery(id+"F0.imprint","IMPRINT",EDGE,{"disambiguationData":[TD([[subQ2,-1.0]])],"derivedFrom":subQ1}),-1.0]])]});}
            var Q94;
            {var subQ0=sQuery(id+"F0.wireOp",EDGE,"E56.top");var subQ7=sQuery(id+"F0.wireOp",EDGE,"E31.0");var subQ9=makeQuery(id+"F0.imprint","INTERSECT",VERTEX,{"derivedFrom":[subQ7,subQ0]});Q94=makeQuery(id+"F0.imprint","IMPRINT",FACE,{"disambiguationData":[TD([[makeQuery(id+"F0.imprint","IMPRINT",EDGE,{"disambiguationData":[TD([[subQ9,-1.0]])],"derivedFrom":subQ7}),1.0]])]});}
            var Q95;
            {var subQ0=sQuery(id+"F0.wireOp",EDGE,"E33.0");var subQ1=sQuery(id+"F0.wireOp",EDGE,"E31.0");var subQ2=makeQuery(id+"F0.imprint","INTERSECT",VERTEX,{"derivedFrom":[subQ1,subQ0]});Q95=makeQuery(id+"F0.imprint","IMPRINT",FACE,{"disambiguationData":[TD([[makeQuery(id+"F0.imprint","IMPRINT",EDGE,{"disambiguationData":[TD([[subQ2,-1.0]])],"derivedFrom":subQ1}),1.0]])]});}
            var Q96;
            {var subQ1=sQuery(id+"F0.wireOp",EDGE,"E31.0");var subQ7=sQuery(id+"F0.wireOp",EDGE,"E34.0");var subQ8=makeQuery(id+"F0.imprint","INTERSECT",VERTEX,{"derivedFrom":[subQ1,subQ7]});Q96=makeQuery(id+"F0.imprint","IMPRINT",FACE,{"disambiguationData":[TD([[makeQuery(id+"F0.imprint","IMPRINT",EDGE,{"disambiguationData":[TD([[subQ8,-1.0]])],"derivedFrom":subQ1}),1.0]])]});}
            var Q97;
            {var subQ1=sQuery(id+"F0.wireOp",EDGE,"E32.0");var subQ7=sQuery(id+"F0.wireOp",EDGE,"E34.0");var subQ8=makeQuery(id+"F0.imprint","INTERSECT",VERTEX,{"derivedFrom":[subQ1,subQ7]});Q97=makeQuery(id+"F0.imprint","IMPRINT",FACE,{"disambiguationData":[TD([[makeQuery(id+"F0.imprint","IMPRINT",EDGE,{"disambiguationData":[TD([[subQ8,-1.0]])],"derivedFrom":subQ1}),-1.0]])]});}
            var Q98;
            {var subQ0=sQuery(id+"F0.wireOp",EDGE,"E32.0");var subQ1=sQuery(id+"F0.wireOp",EDGE,"E0");var subQ2=makeQuery(id+"F0.imprint","INTERSECT",VERTEX,{"derivedFrom":[subQ1,subQ0]});Q98=makeQuery(id+"F0.imprint","IMPRINT",FACE,{"disambiguationData":[TD([[makeQuery(id+"F0.imprint","IMPRINT",EDGE,{"disambiguationData":[TD([[subQ2,-1.0]])],"derivedFrom":subQ0}),-1.0]])]});}
            var Q99;
            {var subQ0=sQuery(id+"F0.wireOp",EDGE,"E34.0");var subQ1=sQuery(id+"F0.wireOp",EDGE,"E1");var subQ2=makeQuery(id+"F0.imprint","INTERSECT",VERTEX,{"derivedFrom":[subQ1,subQ0]});Q99=makeQuery(id+"F0.imprint","IMPRINT",FACE,{"disambiguationData":[TD([[makeQuery(id+"F0.imprint","IMPRINT",EDGE,{"disambiguationData":[TD([[subQ2,-1.0]])],"derivedFrom":subQ0}),-1.0]])]});}
            var Q100;
            {var subQ0=sQuery(id+"F0.wireOp",EDGE,"E34.0");var subQ1=sQuery(id+"F0.wireOp",EDGE,"E1");var subQ2=makeQuery(id+"F0.imprint","INTERSECT",VERTEX,{"derivedFrom":[subQ1,subQ0]});Q100=makeQuery(id+"F0.imprint","IMPRINT",FACE,{"disambiguationData":[TD([[makeQuery(id+"F0.imprint","IMPRINT",EDGE,{"disambiguationData":[TD([[subQ2,1.0]])],"derivedFrom":subQ0}),-1.0]])]});}
            var Q101;
            {var subQ0=sQuery(id+"F0.wireOp",EDGE,"E1");var subQ1=sQuery(id+"F0.wireOp",EDGE,"E0");var subQ2=makeQuery(id+"F0.imprint","INTERSECT",VERTEX,{"derivedFrom":[subQ1,subQ0]});Q101=makeQuery(id+"F0.imprint","IMPRINT",FACE,{"disambiguationData":[TD([[makeQuery(id+"F0.imprint","IMPRINT",EDGE,{"disambiguationData":[TD([[subQ2,1.0]])],"derivedFrom":subQ1}),-1.0]])]});}
            var Q102;
            {var subQ0=sQuery(id+"F0.wireOp",EDGE,"E1");var subQ1=sQuery(id+"F0.wireOp",EDGE,"E0");var subQ2=makeQuery(id+"F0.imprint","INTERSECT",VERTEX,{"derivedFrom":[subQ1,subQ0]});Q102=makeQuery(id+"F0.imprint","IMPRINT",FACE,{"disambiguationData":[TD([[makeQuery(id+"F0.imprint","IMPRINT",EDGE,{"disambiguationData":[TD([[subQ2,-1.0]])],"derivedFrom":subQ1}),1.0]])]});}
            var Q103;
            {var subQ0=sQuery(id+"F0.wireOp",EDGE,"E31.0");var subQ1=sQuery(id+"F0.wireOp",EDGE,"E0");var subQ2=makeQuery(id+"F0.imprint","INTERSECT",VERTEX,{"derivedFrom":[subQ1,subQ0]});Q103=makeQuery(id+"F0.imprint","IMPRINT",FACE,{"disambiguationData":[TD([[makeQuery(id+"F0.imprint","IMPRINT",EDGE,{"disambiguationData":[TD([[subQ2,-1.0]])],"derivedFrom":subQ0}),1.0]])]});}
            extrude(context, id + "F1", {"entities" : qUnion([Q0, Q1, Q2, Q3, Q4, Q5, Q6, Q7, Q8, Q9, Q10, Q11, Q12, Q13, Q14, Q15, Q16, Q17, Q18, Q19, Q20, Q21, Q22, Q23, Q24, Q25, Q26, Q27, Q28, Q29, Q30, Q31, Q32, Q33, Q34, Q35, Q36, Q37, Q38, Q39, Q40, Q41, Q42, Q43, Q44, Q45, Q46, Q47, Q48, Q49, Q50, Q51, Q52, Q53, Q54, Q55, Q56, Q57, Q58, Q59, Q60, Q61, Q62, Q63, Q64, Q65, Q66, Q67, Q68, Q69, Q70, Q71, Q72, Q73, Q74, Q75, Q76, Q77, Q78, Q79, Q80, Q81, Q82, Q83, Q84, Q85, Q86, Q87, Q88, Q89, Q90, Q91, Q92, Q93, Q94, Q95, Q96, Q97, Q98, Q99, Q100, Q101, Q102, Q103]), "depth" : 4 * mm, "offsetDistance" : 25 * mm});
        }
    });
